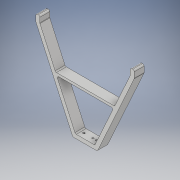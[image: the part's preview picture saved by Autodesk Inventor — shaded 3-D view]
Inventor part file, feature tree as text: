
AUTODESK INVENTOR PART (.ipt)
format: ipt  version: 2019 (Build 230136000, 136)  size: 183,808 bytes
history: native  units: mm
features: sketch x3, extrude x2, fillet x1, hole x1
ambient origin geometry x8: Origin, YZ Plane, XZ Plane, XY Plane, X Axis, Y Axis, Z Axis, Center Point
bodies: Solid1 (feature_tree)
feature tree (7):
  extrude  "Extrusion1"  Depth=180.0mm
  fillet  "Fillet1"  Radius=75.0mm
  hole  "Hole1"  [1 undecoded]
  extrude  "Extrusion2"  Depth=8.0mm
  sketch  "Sketch2"  dims[d0=200.0mm d1=180.0mm d2=75.0mm]
  sketch  "Sketch5"  dims[d3=50.0mm d4=15.0mm]
  sketch  "Sketch6"  dims[d5=15.0mm d6=8.0mm d7=8.0mm d10=77.0mm d11=8.0mm d12=8.0mm d13=5.0mm d14=8.0mm d15=5.0mm d16=20.0mm d17=0.0mm d18=3.0mm d39=1.0mm d40=18.0mm d41=7.0mm d42=10.0mm d43=40.2055mm d44=3.5mm d45=6.0mm d46=4.0mm d47=2.0mm d48=90.0deg d49=8.0mm d50=20.594885mm d51=8.0mm d52=0.0mm d34=1.0mm d35=1.0mm d36=1.0mm d37=0.15mm d38=0.25mm]
note: 1 required parameter value undecoded (feature->parameter linkage not recoverable at this tier; creation-order binding heuristic only, values carry confidence <= 0.55)
